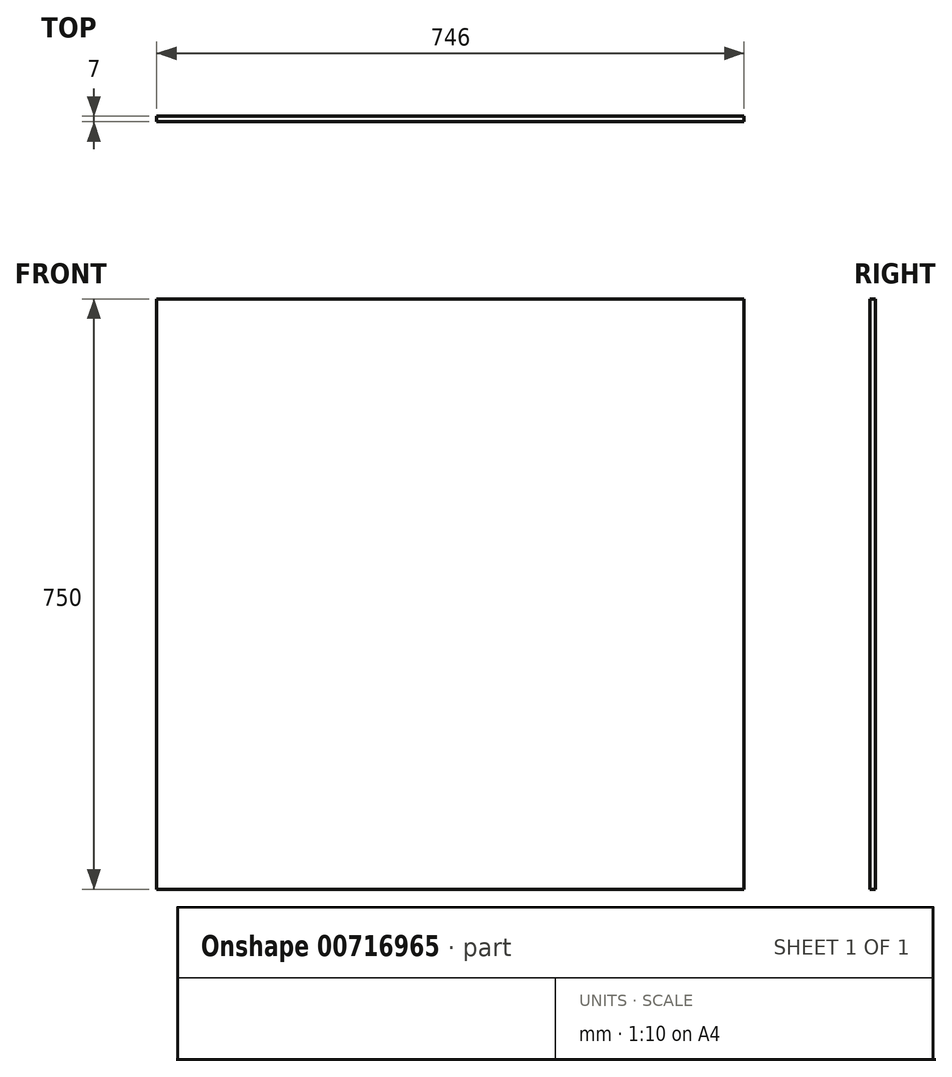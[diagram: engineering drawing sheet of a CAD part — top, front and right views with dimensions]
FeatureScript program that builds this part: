
annotation { "Feature Type Name" : "Feature", "Feature Type Description" : "" }
export const myFeature = defineFeature(function(context is Context, id is Id, definition is map)
    precondition{}
    {
        {
            var Q0;
            Q0=qCreatedBy(makeId("Front.planeOp"),FACE);
            var sketch = newSketch(context, id + "F0", { "sketchPlane" : qUnion([Q0])});
            skLineSegment(sketch, "E0.bottom", {"start": v(373, 375) * mm, "end": v(-373, 375) * mm});
            skLineSegment(sketch, "E0.top", {"start": v(373, -375) * mm, "end": v(-373, -375) * mm});
            skLineSegment(sketch, "E0.left", {"start": v(373, 375) * mm, "end": v(373, -375) * mm});
            skLineSegment(sketch, "E0.right", {"start": v(-373, 375) * mm, "end": v(-373, -375) * mm});
            skPoint(sketch, "E0.middle", {"position": v(0, 0) * mm});
            skSolve(sketch);
        }
        {
            var Q0;
            Q0=makeQuery(id+"F0.imprint","IMPRINT",FACE,{"disambiguationData":[TD([[makeQuery(id+"F0.imprint","IMPRINT",EDGE,{"derivedFrom":sQuery(id+"F0.wireOp",EDGE,"E0.bottom")}),1.0]])]});
            extrude(context, id + "F1", {"entities" : qUnion([Q0]), "depth" : 7 * mm, "offsetDistance" : 25 * mm});
        }
    });
